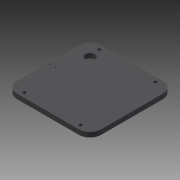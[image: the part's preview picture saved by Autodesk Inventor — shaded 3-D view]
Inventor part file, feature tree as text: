
AUTODESK INVENTOR PART (.ipt)
format: ipt  version: 2013 (Build 170138000, 138)  size: 143,872 bytes
history: native  units: mm
features: sketch x5, extrude x4, fillet x1, hole x1
ambient origin geometry x8: Origin, YZ Plane, XZ Plane, XY Plane, X Axis, Y Axis, Z Axis, Center Point
bodies: Solid1 (feature_tree)
feature tree (11):
  extrude  "Extrusion1"  Depth=225.0mm
  fillet  "Fillet1"  Radius=225.0mm
  extrude  "Extrusion2"  Depth=37.5mm
  hole  "Hole1"  [1 undecoded]
  extrude  "Extrusion4"  Depth=30.0mm
  extrude  "Extrusion5"  Depth=2.0mm TaperAngle=0.0deg
  sketch  "Sketch1"  dims[d0=200.0mm d2=225.0mm d3=225.0mm]
  sketch  "Sketch2"  dims[d4=150.0mm d5=37.5mm]
  sketch  "Sketch4"  dims[d6=12.5mm d7=8.1mm]
  sketch  "Sketch5"  dims[d8=12.7mm d9=0.0mm d13=30.0mm]
  sketch  "Sketch6"  dims[d14=200.0mm d16=2.0mm d17=0.0mm d25=3.4mm d26=6.0mm d27=6.5mm d28=4.5mm d29=14.3117mm d30=8.0mm d31=20.594885mm d32=25.0mm d35=45.0deg d37=10.0mm d38=0.0mm d39=50.0mm d42=3.0mm d43=0.0mm d44=15.0mm d45=0.0mm d46=5.0mm d47=3.1mm]
note: 1 required parameter value undecoded (feature->parameter linkage not recoverable at this tier; creation-order binding heuristic only, values carry confidence <= 0.55)
